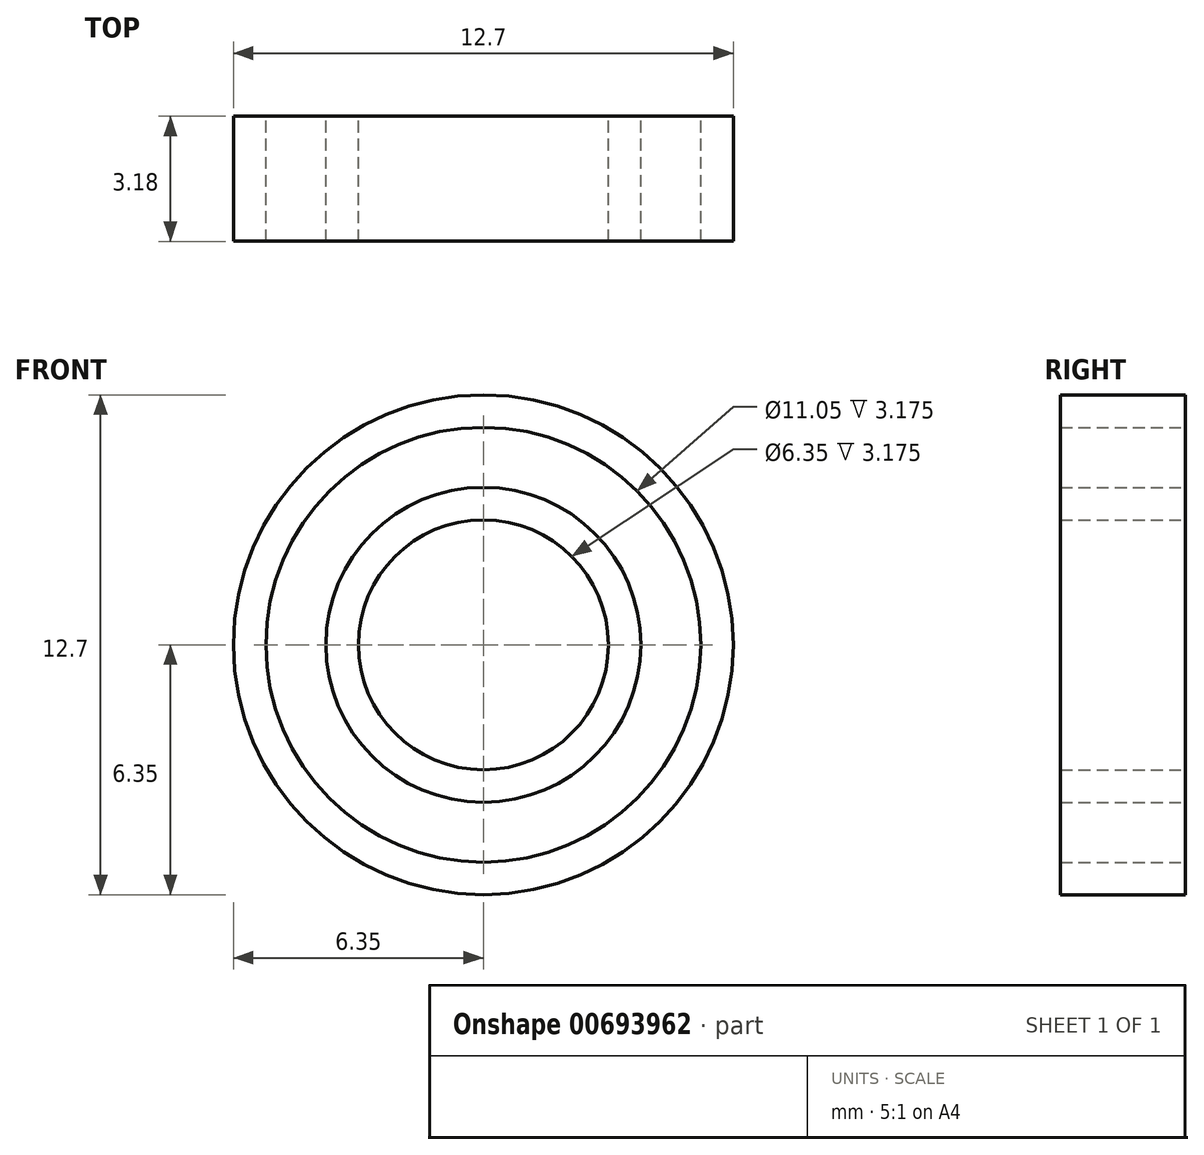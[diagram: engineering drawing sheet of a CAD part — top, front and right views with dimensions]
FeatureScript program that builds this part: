
annotation { "Feature Type Name" : "Feature", "Feature Type Description" : "" }
export const myFeature = defineFeature(function(context is Context, id is Id, definition is map)
    precondition{}
    {
        {
            var Q0;
            Q0=qCreatedBy(makeId("Front.planeOp"),FACE);
            var sketch = newSketch(context, id + "F0", { "sketchPlane" : qUnion([Q0])});
            skCircle(sketch, "E0", {"center": v(0, 0) * mm, "radius": 6.35 * mm});
            skCircle(sketch, "E1", {"center": v(0, 0) * mm, "radius": 5.52 * mm});
            skCircle(sketch, "E2", {"center": v(0, 0) * mm, "radius": 3.17 * mm});
            skCircle(sketch, "E3", {"center": v(0, 0) * mm, "radius": 4 * mm});
            skPoint(sketch, "E4.center", {"position": v(0, -0.03) * mm});
            skLineSegment(sketch, "E5", {"start": v(5.52, -0.05) * mm, "end": v(5.52, -0.05) * mm});
            skSolve(sketch);
        }
        {
            var Q0;
            Q0 = qSketchRegion(id + "F0", true);
            var Q1;
            Q1=makeQuery(id+"F0.imprint","IMPRINT",FACE,{"disambiguationData":[TD([[makeQuery(id+"F0.imprint","IMPRINT",EDGE,{"derivedFrom":sQuery(id+"F0.wireOp",EDGE,"E2")}),-1.0]])]});
            extrude(context, id + "F1", {"entities" : qUnion([Q0, Q1]), "depth" : 3.17 * mm, "offsetDistance" : 25 * mm});
        }
    });
